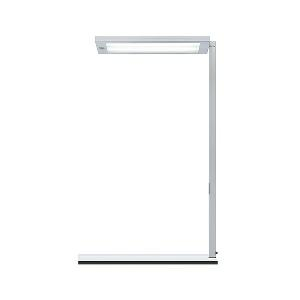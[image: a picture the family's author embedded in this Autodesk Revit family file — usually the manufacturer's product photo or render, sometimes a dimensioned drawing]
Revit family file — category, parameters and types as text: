
# Revit family: lavigo_-_dpt_14000_vtl_r_g2_00804512_79c3
name_source: partatom
category: Lighting Fixtures
units: mm (PartAtom-declared; Revit-internal decimal feet)

## family parameters
Cut with Voids When Loaded = No
Host = Face
Light Source = No
Part Type = Normal
Room Calculation Point = No
Round Connector Dimension = Use Diameter
Shared = No

## types (1)
- LAVIGO - DPT 14000/VTL/R/G2 (1 x LED VTL, 14250 lm, 3000-6500K)
    Apparent Load = 100 VA
    Approval mark = CE
    CIE Flux Codes = 60 87 97 12 100
    Color Rendering = 80-89
    Color Temperature = 3000-6500K
    Control Gear = Electronic ballast
    Default Elevation = 1800 mm
    Description = DPT 14000/VTL/R/G2|Desk-mounted luminaire|light source: LED|work equipment: Electronic ballast|connected load: 220-240 V, 50/60 Hz|Power consumption: approx. 100 W|standby: approx. 0,50|power factor: approx. 0,965|luminous flux: 14250 lm|luminous efficacy: 142 lm/W|light distribution: Direct/indirect|direct ratio: approx. 12 %|colour temperature: , ca. 2700-6500 K|color rendering index (CRI): >= 80|technology: Presence and daylight sensor control (PIR)|operation: Multi-function switch|luminaire body|material: Steel/plastic|surface: Painted|colour: White|lamp cover: Acrylic (PMMA), Satine|tubular section|material: Steel tube|surface: Painted|Form: Tubular section upright|colour of tubular section: White|weight (net): approx. 15.4 kg|mains lead: 3.70 m Mains plug CEE 7/VII|Fastening: Socket, Table adaptor|decorative contrast side parts: Flint grey|glare control: Prism aperture|luminance(L65): <= 3000 cd/m|unified glare rating(4H 8H): <=  16|special features: Luminaire head detachable, Cradle to Cradle Certified TM, Direct light component with edge light and light-guide technology for homogenous light exit, Flicker-free, Indirect light component biodynamic light VTL, direct light component neutral working light, Integrated light and presence sensor PIR, Integrated light management for biodynamic light VTL, Retrofittable with TALK module, Inclination of tubular section adjustable, Separated, direct and indirect light individually adjustable|
    Frequency = 50 Hz, 60 Hz
    Height = 36 mm
    Lamp = 1 x LED VTL
    Lamp Light Flux = 14250 lm
    Lamp count = 1
    Length = 675 mm
    Luminous efficacy = 143 lm/W
    Manufacturer = Waldmann
    ModVariant = No
    Model = 00804512
    Mounting Place = Table
    Mounting Type = Surface mounted
    Number of Poles = 1
    OnlyDefault = Yes
    Power Factor = 1
    Product Name = LAVIGO - DPT 14000/VTL/R/G2
    Product group = Desk mounted luminaire with detector
    ProductGroupID = 2201
    Protection Class = Protection class I
    Protection Degree = IP 20
    RLX_Detail_Level = 1
    RLX_Emergency_Light_Flux = 0 lm
    RLX_Emergency_Type = 0
    RLX_Emergency_Type_DB = No
    RlxData = <blob elided: 35285 chars, md5=bd5f4482>
    Socket = socket
    Standby Power = 0 W
    System Light Flux = 14250 lm
    System Power = 100 W
    Type Comments = Product without accessories
    Type Image = 121716000-00630762.jpg
    URL = http://relux.com
    VarID = ---
    Voltage = 230 V
    Voltage Range = 220-240 V
    Weight = 0.00 kg
    Width = 320 mm

## geometry (parser evidence)
native form markers: Blend x4, Sweep x15
no freeform markers — native parametric forms only
